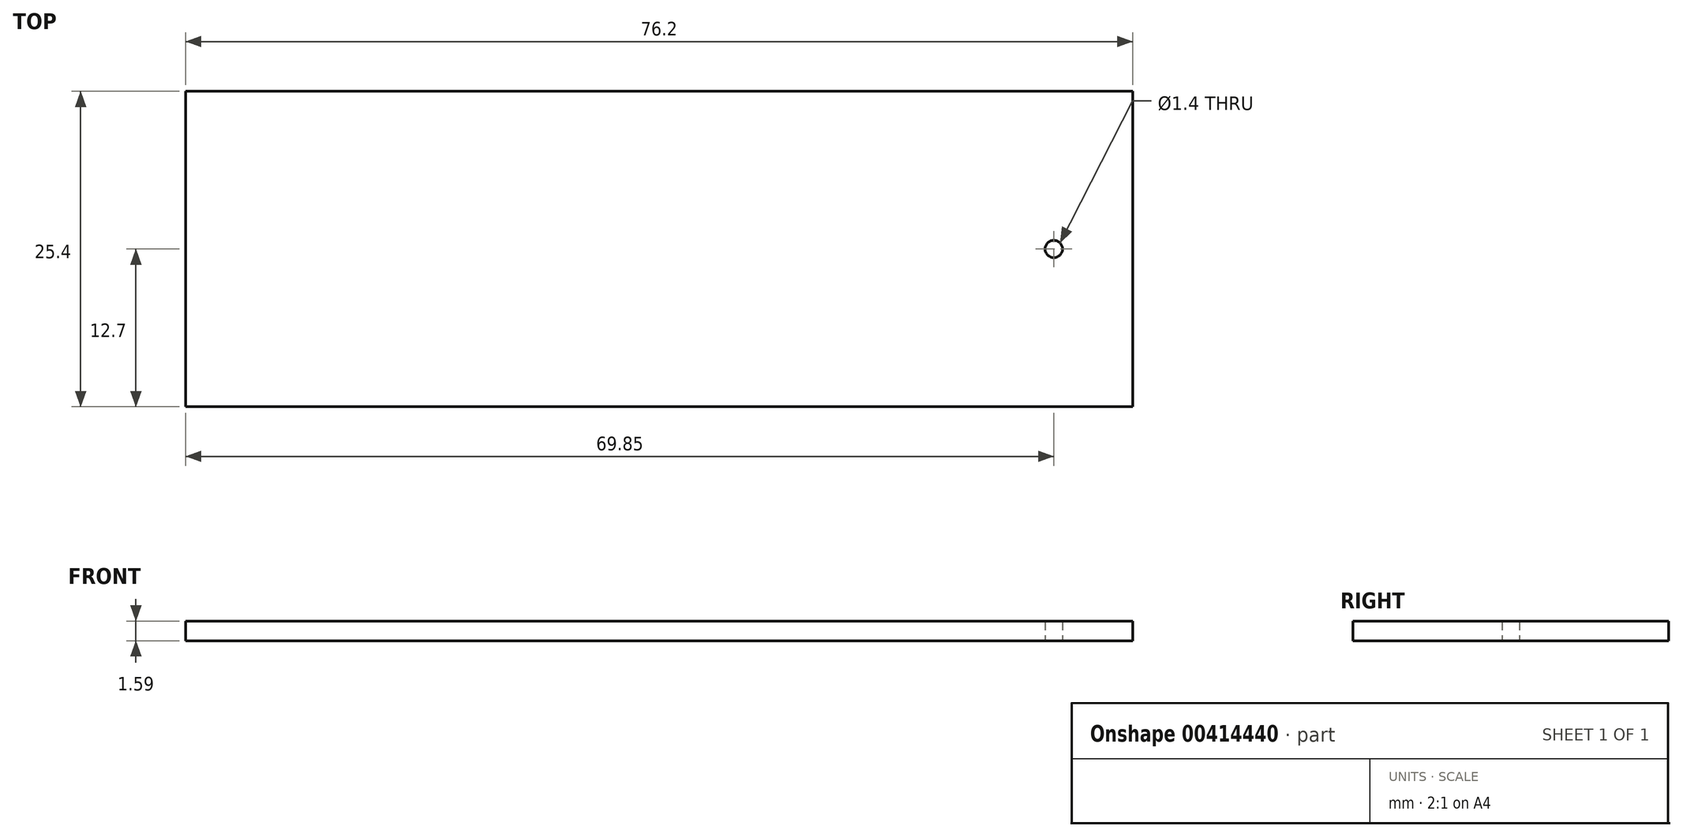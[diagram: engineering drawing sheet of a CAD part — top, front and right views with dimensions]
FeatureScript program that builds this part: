
annotation { "Feature Type Name" : "Feature", "Feature Type Description" : "" }
export const myFeature = defineFeature(function(context is Context, id is Id, definition is map)
    precondition{}
    {
        {
            var Q0;
            Q0=qCreatedBy(makeId("Top.planeOp"),FACE);
            var sketch = newSketch(context, id + "F0", { "sketchPlane" : qUnion([Q0])});
            skLineSegment(sketch, "E0.bottom", {"start": v(0, -12.7) * mm, "end": v(-76.2, -12.7) * mm});
            skLineSegment(sketch, "E0.top", {"start": v(0, 12.7) * mm, "end": v(-76.2, 12.7) * mm});
            skLineSegment(sketch, "E0.left", {"start": v(0, -12.7) * mm, "end": v(0, 12.7) * mm});
            skLineSegment(sketch, "E0.right", {"start": v(-76.2, -12.7) * mm, "end": v(-76.2, 12.7) * mm});
            skCircle(sketch, "E1", {"center": v(-6.35, 0) * mm, "radius": 0.7 * mm});
            skSolve(sketch);
        }
        {
            var Q0;
            Q0 = qSketchRegion(id + "F0", true);
            extrude(context, id + "F1", {"entities" : qUnion([Q0]), "depth" : 1.59 * mm});
        }
    });
